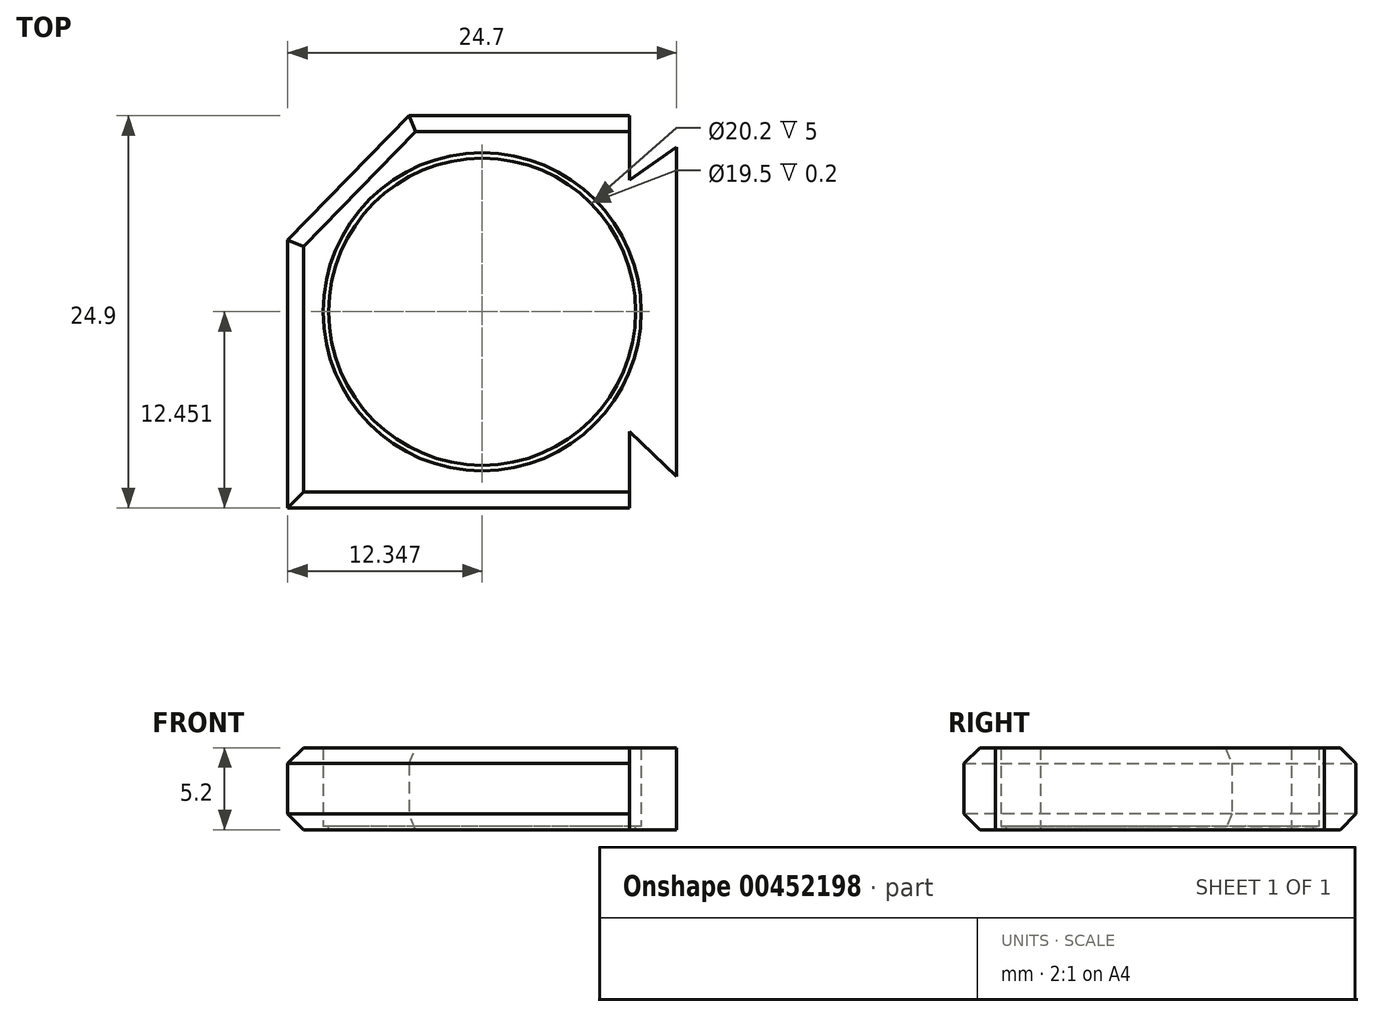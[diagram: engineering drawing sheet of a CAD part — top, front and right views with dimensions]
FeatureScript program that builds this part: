
annotation { "Feature Type Name" : "Feature", "Feature Type Description" : "" }
export const myFeature = defineFeature(function(context is Context, id is Id, definition is map)
    precondition{}
    {
        {
            var Q0;
            Q0=qCreatedBy(makeId("Top.planeOp"),FACE);
            var sketch = newSketch(context, id + "F0", { "sketchPlane" : qUnion([Q0])});
            skLineSegment(sketch, "E0.bottom", {"start": v(8.68, -12.52) * mm, "end": v(-16.02, -12.52) * mm});
            skLineSegment(sketch, "E0.top", {"start": v(8.68, 12.38) * mm, "end": v(-16.02, 12.38) * mm});
            skLineSegment(sketch, "E0.left", {"start": v(8.68, -12.52) * mm, "end": v(8.68, 12.38) * mm});
            skLineSegment(sketch, "E0.right", {"start": v(-16.02, -12.52) * mm, "end": v(-16.02, 12.38) * mm});
            skPoint(sketch, "E0.middle", {"position": v(-3.67, -0.07) * mm});
            skCircle(sketch, "E1", {"center": v(-3.67, -0.07) * mm, "radius": 9.75 * mm});
            skCircle(sketch, "E2", {"center": v(-3.67, -0.07) * mm, "radius": 10.1 * mm});
            skLineSegment(sketch, "E3", {"start": v(5.68, -7.66) * mm, "end": v(5.68, -12.52) * mm});
            skLineSegment(sketch, "E4", {"start": v(5.68, 8.28) * mm, "end": v(5.68, 12.38) * mm});
            skLineSegment(sketch, "E5", {"start": v(5.68, 8.28) * mm, "end": v(8.68, 10.38) * mm});
            skLineSegment(sketch, "E6", {"start": v(5.68, -7.66) * mm, "end": v(8.68, -10.52) * mm});
            skLineSegment(sketch, "E7", {"start": v(-8.32, 12.38) * mm, "end": v(-16.02, 4.48) * mm});
            skSolve(sketch);
        }
        {
            var Q0;
            Q0=makeQuery(id+"F0.imprint","IMPRINT",FACE,{"disambiguationData":[TD([[makeQuery(id+"F0.imprint","IMPRINT",EDGE,{"derivedFrom":sQuery(id+"F0.wireOp",EDGE,"E2")}),-1.0]])]});
            extrude(context, id + "F1", {"entities" : qUnion([Q0]), "depth" : 5 * mm, "offsetDistance" : 25 * mm});
        }
        {
            var Q0;
            Q0=makeQuery(id+"F0.imprint","IMPRINT",FACE,{"disambiguationData":[TD([[makeQuery(id+"F0.imprint","IMPRINT",EDGE,{"derivedFrom":sQuery(id+"F0.wireOp",EDGE,"E1")}),-1.0]])]});
            var Q1;
            Q1=makeQuery(id+"F0.imprint","IMPRINT",FACE,{"disambiguationData":[TD([[makeQuery(id+"F0.imprint","IMPRINT",EDGE,{"derivedFrom":sQuery(id+"F0.wireOp",EDGE,"E2")}),-1.0]])]});
            extrude(context, id + "F2", {"entities" : qUnion([Q0, Q1]), "operationType" : NewBodyOperationType.ADD, "oppositeDirection" : true, "depth" : 0.2 * mm, "offsetDistance" : 25 * mm});
        }
        {
            var Q0;
            Q0=makeQuery(id+"F1.opExtrude","CAP_EDGE",EDGE,{"disambiguationData":[OSD([sQuery(id+"F0.wireOp",EDGE,"E0.bottom")])],"isStart":false});
            var Q1;
            Q1=makeQuery(id+"F1.opExtrude","CAP_EDGE",EDGE,{"disambiguationData":[OSD([sQuery(id+"F0.wireOp",EDGE,"E0.right")])],"isStart":false});
            var Q2;
            Q2=makeQuery(id+"F1.opExtrude","CAP_EDGE",EDGE,{"disambiguationData":[OSD([sQuery(id+"F0.wireOp",EDGE,"E7")])],"isStart":false});
            var Q3;
            Q3=makeQuery(id+"F1.opExtrude","CAP_EDGE",EDGE,{"disambiguationData":[OSD([sQuery(id+"F0.wireOp",EDGE,"E0.top")])],"isStart":false});
            var Q4;
            Q4=makeQuery(id+"F2.opExtrude","CAP_EDGE",EDGE,{"disambiguationData":[OSD([sQuery(id+"F0.wireOp",EDGE,"E0.top")])],"isStart":false});
            var Q5;
            Q5=makeQuery(id+"F2.opExtrude","CAP_EDGE",EDGE,{"disambiguationData":[OSD([sQuery(id+"F0.wireOp",EDGE,"E7")])],"isStart":false});
            var Q6;
            Q6=makeQuery(id+"F2.opExtrude","CAP_EDGE",EDGE,{"disambiguationData":[OSD([sQuery(id+"F0.wireOp",EDGE,"E0.right")])],"isStart":false});
            var Q7;
            Q7=makeQuery(id+"F2.opExtrude","CAP_EDGE",EDGE,{"disambiguationData":[OSD([sQuery(id+"F0.wireOp",EDGE,"E0.bottom")])],"isStart":false});
            chamfer(context, id + "F3", {"entities" : qUnion([Q0, Q1, Q2, Q3, Q4, Q5, Q6, Q7]), "width" : 1 * mm, "tangentPropagation" : true});
        }
    });
